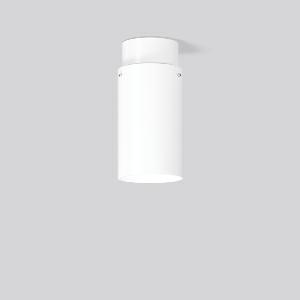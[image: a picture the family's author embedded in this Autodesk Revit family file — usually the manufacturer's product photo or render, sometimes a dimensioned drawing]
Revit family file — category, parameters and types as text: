
# Revit family: glasdownlight_931178_002_1_76_8f3b
name_source: partatom
category: Lighting Fixtures
units: mm (PartAtom-declared; Revit-internal decimal feet)

## family parameters
Cut with Voids When Loaded = No
Host = Face
Light Source = No
Part Type = Normal
Room Calculation Point = No
Round Connector Dimension = Use Diameter
Shared = No

## types (1)
- GLASDOWNLIGHT (1 x LED Modul 840, 3000 lm, 4000)
    Apparent Load = 24 VA
    CIE Flux Codes = 28 54 78 61 100
    Color Rendering = 80
    Color Temperature = 4000
    Default Elevation = 1800 mm
    Description = Series: GLASDOWNLIGHT
Decorative round surface-mounted luminaire. Base: aluminium, powder-coated. Mouth blown 3-layer opal glass (Triplex glass) with satin finish. Glass fastening: retaining screws. Triplex glass produces particularly homogeneous, soft and glare free lighting. 
Colour: white
Diameter: 150 mm
Height: 300 mm
Lamp: LED
Socket: without socket
Colour temperature: 4000K
Colour rendering index (CRI): 80
System power: 24 W
Rated luminous flux: 3000 lm
Luminous efficiency: 125 lm/W
Control gear: Converter, dimmable, DALI
Protection class: I
Type of protection: IP 20
    Height = 300 mm
    Lamp = 1 x LED Modul 840
    Lamp Light Flux = 3000 lm
    Lamp count = 1
    Length = 150 mm
    Lifetime = 50000 h
    Luminous efficacy = 125 lm/W
    Manufacturer = RZB
    ModVariant = No
    Model = 931178.002.1.76
    Mounting Place = Ceiling
    Mounting Type = Surface mounted
    Number of Poles = 1
    OnlyDefault = Yes
    Power Factor = 1
    Product Name = GLASDOWNLIGHT
    Product group = Surface mounted ceiling luminaires
    ProductGroupID = 303
    Protection Class = Protection class I
    Protection Degree = IP 20
    RLX_Detail_Level = 1
    RLX_Emergency_Light_Flux = 0 lm
    RLX_Emergency_Type = 0
    RLX_Emergency_Type_DB = No
    RlxData = <blob elided: 14137 chars, md5=4bd6812f>
    Socket = socket
    Standby Power = 0 W
    System Light Flux = 3000 lm
    System Power = 24 W
    Type Comments = Product without accessories
    Type Image = 931178.002.jpg
    URL = http://relux.com
    VarID = ---
    Voltage = 230 V
    Voltage Range = 220-240 V
    Weight = 0.00 kg
    Width = 0 mm  [stored 0 ft]

note: [stored X ft] marks values corroborated as IEEE doubles in the binary element streams (Revit-internal decimal feet)

## geometry (parser evidence)
native form markers: Sweep x14
no freeform markers — native parametric forms only
